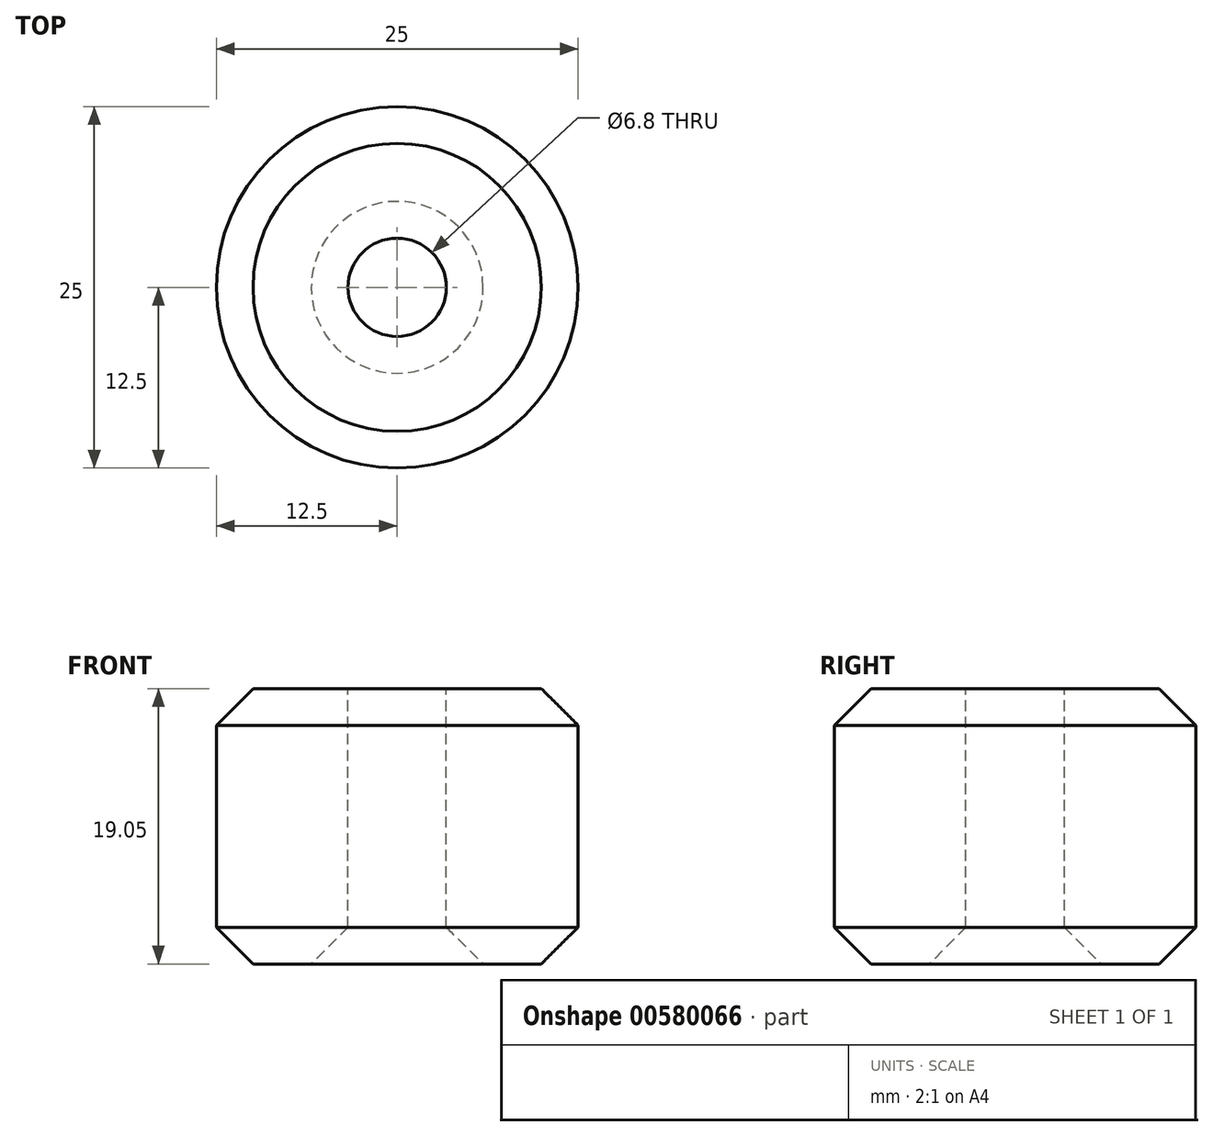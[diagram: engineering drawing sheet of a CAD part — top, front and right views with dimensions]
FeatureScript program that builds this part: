
annotation { "Feature Type Name" : "Feature", "Feature Type Description" : "" }
export const myFeature = defineFeature(function(context is Context, id is Id, definition is map)
    precondition{}
    {
        {
            var Q0;
            Q0=qCreatedBy(makeId("Top.planeOp"),FACE);
            var sketch = newSketch(context, id + "F0", { "sketchPlane" : qUnion([Q0])});
            skCircle(sketch, "E0", {"center": v(0, 0) * mm, "radius": 12.5 * mm});
            skSolve(sketch);
        }
        {
            var Q0;
            Q0 = qSketchRegion(id + "F0", true);
            extrude(context, id + "F1", {"entities" : qUnion([Q0]), "depth" : 19.05 * mm, "offsetDistance" : 25.4 * mm});
        }
        {
            var Q0;
            Q0=makeQuery(id+"F1.opExtrude","CAP_FACE",FACE,{"disambiguationData":[OSD([sQuery(id+"F0.wireOp",EDGE,"E0")])],"isStart":false});
            var sketch = newSketch(context, id + "F2", { "sketchPlane" : qUnion([Q0])});
            skCircle(sketch, "E1", {"center": v(0, 0) * mm, "radius": 3.4 * mm});
            skSolve(sketch);
        }
        {
            var Q0;
            Q0 = qSketchRegion(id + "F2", true);
            extrude(context, id + "F3", {"entities" : qUnion([Q0]), "operationType" : NewBodyOperationType.REMOVE, "oppositeDirection" : true, "depth" : 25.4 * mm, "offsetDistance" : 25.4 * mm});
        }
        {
            var Q0;
            Q0=makeQuery(id+"F3.boolean.opBoolean","COPY",EDGE,{"derivedFrom":makeQuery(id+"F3.opExtrude","CAP_EDGE",EDGE,{"disambiguationData":[OSD([sQuery(id+"F2.wireOp",EDGE,"E1")])],"isStart":true})});
            var Q1;
            Q1=makeQuery(id+"F3.boolean.opBoolean","INTERSECT",EDGE,{"derivedFrom":[makeQuery(id+"F1.opExtrude","CAP_FACE",FACE,{"disambiguationData":[OSD([sQuery(id+"F0.wireOp",EDGE,"E0")])],"isStart":true}),makeQuery(id+"F3.opExtrude","SWEPT_FACE",FACE,{"disambiguationData":[OSD([sQuery(id+"F2.wireOp",EDGE,"E1")])]})]});
            var Q2;
            Q2=makeQuery(id+"F1.opExtrude","CAP_EDGE",EDGE,{"disambiguationData":[OSD([sQuery(id+"F0.wireOp",EDGE,"E0")])],"isStart":true});
            var Q3;
            Q3=makeQuery(id+"F1.opExtrude","CAP_EDGE",EDGE,{"disambiguationData":[OSD([sQuery(id+"F0.wireOp",EDGE,"E0")])],"isStart":false});
            chamfer(context, id + "F4", {"entities" : qUnion([Q0, Q1, Q2, Q3]), "width" : 2.54 * mm, "tangentPropagation" : true});
        }
    });
